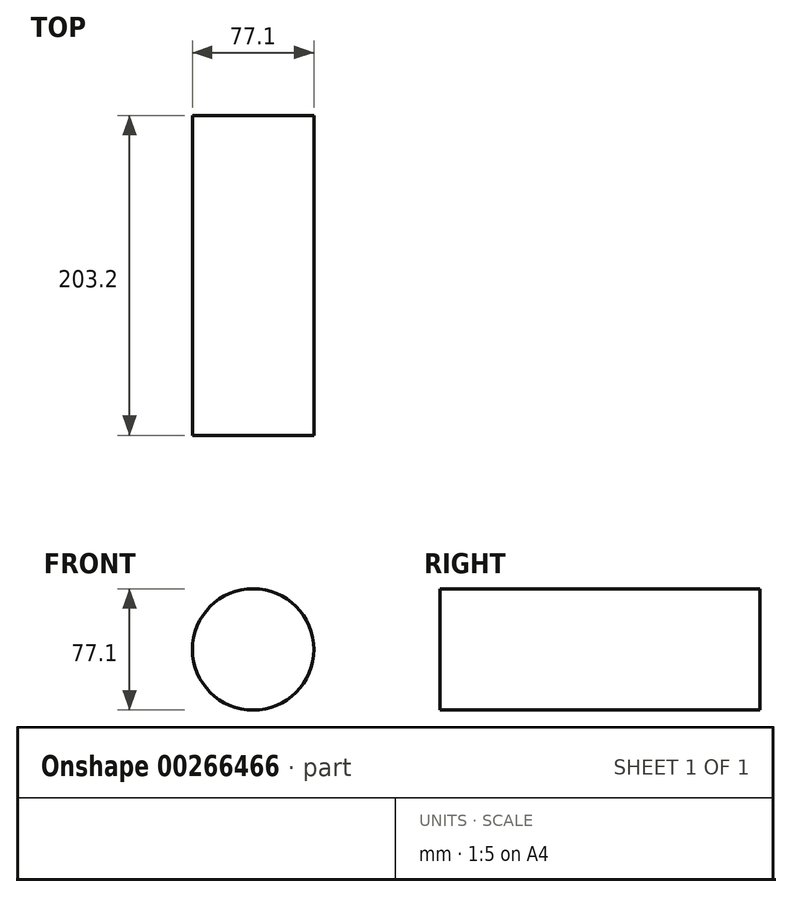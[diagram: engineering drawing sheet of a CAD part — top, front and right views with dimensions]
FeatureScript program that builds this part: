
annotation { "Feature Type Name" : "Feature", "Feature Type Description" : "" }
export const myFeature = defineFeature(function(context is Context, id is Id, definition is map)
    precondition{}
    {
        {
            var Q0;
            Q0=qCreatedBy(makeId("Front.planeOp"),FACE);
            var sketch = newSketch(context, id + "F0", { "sketchPlane" : qUnion([Q0])});
            skCircle(sketch, "E0", {"center": v(0, 0) * mm, "radius": 38.55 * mm});
            skSolve(sketch);
        }
        {
            var Q0;
            Q0 = qSketchRegion(id + "F0", true);
            extrude(context, id + "F1", {"entities" : qUnion([Q0]), "depth" : 203.2 * mm});
        }
    });
